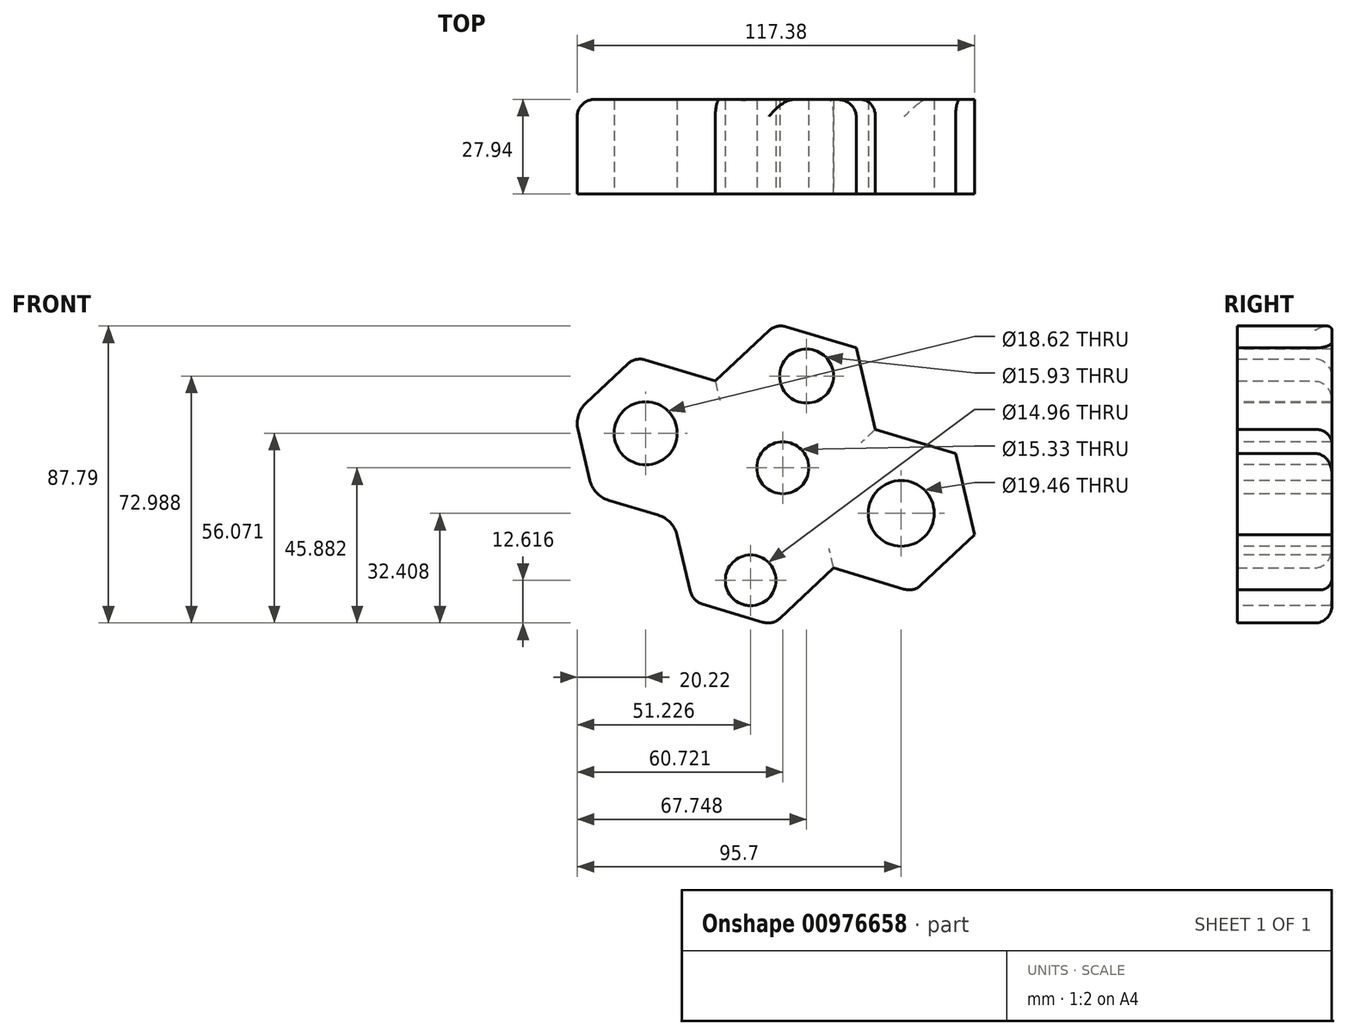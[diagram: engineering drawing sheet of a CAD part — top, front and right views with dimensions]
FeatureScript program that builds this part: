
annotation { "Feature Type Name" : "Feature", "Feature Type Description" : "" }
export const myFeature = defineFeature(function(context is Context, id is Id, definition is map)
    precondition{}
    {
        {
            var Q0;
            Q0=qCreatedBy(makeId("Front.planeOp"),FACE);
            var sketch = newSketch(context, id + "F0", { "sketchPlane" : qUnion([Q0])});
            skCircle(sketch, "E0.cCircle", {"center": v(-72.92, 28.26) * mm, "radius": 21.4 * mm, "construction": true});
            skLineSegment(sketch, "E0.0", {"start": v(-49.27, 21.14) * mm, "end": v(-67.26, 4.22) * mm});
            skLineSegment(sketch, "E0.1", {"start": v(-67.26, 4.22) * mm, "end": v(-90.91, 11.34) * mm});
            skLineSegment(sketch, "E0.2", {"start": v(-90.91, 11.34) * mm, "end": v(-96.57, 35.38) * mm});
            skLineSegment(sketch, "E0.3", {"start": v(-96.57, 35.38) * mm, "end": v(-78.57, 52.3) * mm});
            skLineSegment(sketch, "E0.4", {"start": v(-78.57, 52.3) * mm, "end": v(-54.92, 45.18) * mm});
            skLineSegment(sketch, "E0.5", {"start": v(-54.92, 45.18) * mm, "end": v(-49.27, 21.14) * mm});
            skPoint(sketch, "E0.0.midPoint", {"position": v(-58.26, 12.68) * mm});
            skLineSegment(sketch, "E1.MirrorCS", {"start": v(-36.93, 62.1) * mm, "end": v(-54.92, 45.18) * mm});
            skCircle(sketch, "E2.MirrorC", {"center": v(-31.27, 38.06) * mm, "radius": 21.4 * mm, "construction": true});
            skLineSegment(sketch, "E3.MirrorCS", {"start": v(-13.28, 54.98) * mm, "end": v(-36.93, 62.1) * mm});
            skLineSegment(sketch, "E4.MirrorCS", {"start": v(-7.62, 30.93) * mm, "end": v(-13.28, 54.98) * mm});
            skLineSegment(sketch, "E5.MirrorCS", {"start": v(-25.62, 14.01) * mm, "end": v(-7.62, 30.93) * mm});
            skLineSegment(sketch, "E6.MirrorCS", {"start": v(-49.27, 21.14) * mm, "end": v(-25.62, 14.01) * mm});
            skLineSegment(sketch, "E7.MirrorCS", {"start": v(-49.27, 21.14) * mm, "end": v(-54.92, 45.18) * mm});
            skLineSegment(sketch, "E8.MirrorCS", {"start": v(-25.62, 14.01) * mm, "end": v(-19.96, -10.03) * mm});
            skCircle(sketch, "E9.MirrorC", {"center": v(-43.61, -2.9) * mm, "radius": 21.4 * mm, "construction": true});
            skLineSegment(sketch, "E10.MirrorCS", {"start": v(-19.96, -10.03) * mm, "end": v(-37.95, -26.95) * mm});
            skLineSegment(sketch, "E11.MirrorCS", {"start": v(-37.95, -26.95) * mm, "end": v(-61.6, -19.83) * mm});
            skLineSegment(sketch, "E12.MirrorCS", {"start": v(-61.6, -19.83) * mm, "end": v(-67.26, 4.22) * mm});
            skCircle(sketch, "E13.MirrorC", {"center": v(-1.97, 6.89) * mm, "radius": 21.4 * mm, "construction": true});
            skLineSegment(sketch, "E14.MirrorCS", {"start": v(3.69, -17.15) * mm, "end": v(21.68, -0.23) * mm});
            skLineSegment(sketch, "E15.MirrorCS", {"start": v(21.68, -0.23) * mm, "end": v(16.03, 23.8) * mm});
            skLineSegment(sketch, "E16.MirrorCS", {"start": v(-7.62, 30.93) * mm, "end": v(16.03, 23.8) * mm});
            skLineSegment(sketch, "E17.MirrorCS", {"start": v(-7.62, 30.93) * mm, "end": v(-25.62, 14.01) * mm});
            skLineSegment(sketch, "E18.MirrorCS", {"start": v(-19.96, -10.03) * mm, "end": v(3.69, -17.15) * mm});
            skSolve(sketch);
        }
        {
            var Q0;
            Q0 = qSketchRegion(id + "F0", true);
            extrude(context, id + "F1", {"entities" : qUnion([Q0]), "depth" : 27.94 * mm, "offsetDistance" : 25.4 * mm});
        }
        {
            var Q0;
            Q0=makeQuery(id+"F1.opExtrude","CAP_FACE",FACE,{"disambiguationData":[OSD([sQuery(id+"F0.wireOp",EDGE,"E0.1"),sQuery(id+"F0.wireOp",EDGE,"E0.2"),sQuery(id+"F0.wireOp",EDGE,"E0.3"),sQuery(id+"F0.wireOp",EDGE,"E0.4"),sQuery(id+"F0.wireOp",EDGE,"E1.MirrorCS"),sQuery(id+"F0.wireOp",EDGE,"E3.MirrorCS"),sQuery(id+"F0.wireOp",EDGE,"E4.MirrorCS"),sQuery(id+"F0.wireOp",EDGE,"E10.MirrorCS"),sQuery(id+"F0.wireOp",EDGE,"E11.MirrorCS"),sQuery(id+"F0.wireOp",EDGE,"E12.MirrorCS"),sQuery(id+"F0.wireOp",EDGE,"E14.MirrorCS"),sQuery(id+"F0.wireOp",EDGE,"E15.MirrorCS"),sQuery(id+"F0.wireOp",EDGE,"E16.MirrorCS"),sQuery(id+"F0.wireOp",EDGE,"E18.MirrorCS")])],"isStart":false});
            var sketch = newSketch(context, id + "F2", { "sketchPlane" : qUnion([Q0])});
            skCircle(sketch, "E19", {"center": v(0, 6.09) * mm, "radius": 9.73 * mm});
            skCircle(sketch, "E20", {"center": v(-75.48, 29.75) * mm, "radius": 9.31 * mm});
            skCircle(sketch, "E21", {"center": v(-27.95, 46.67) * mm, "radius": 7.97 * mm});
            skCircle(sketch, "E22", {"center": v(-44.47, -13.7) * mm, "radius": 7.48 * mm});
            skCircle(sketch, "E23", {"center": v(-34.98, 19.56) * mm, "radius": 7.67 * mm});
            skSolve(sketch);
        }
        {
            var Q0;
            Q0 = qSketchRegion(id + "F2", true);
            extrude(context, id + "F3", {"entities" : qUnion([Q0]), "operationType" : NewBodyOperationType.REMOVE, "oppositeDirection" : true, "depth" : 54.86 * mm, "offsetDistance" : 25.4 * mm});
        }
        {
            var Q0;
            Q0=makeQuery(id+"F1.opExtrude","SWEPT_EDGE",EDGE,{"disambiguationData":[OSD([sQuery(id+"F0.wireOp",EDGE,"E0.1"),sQuery(id+"F0.wireOp",EDGE,"E12.MirrorCS"),sQuery(id+"F0.wireOp",EDGE,"E0.0")])]});
            var Q1;
            Q1=makeQuery(id+"F1.opExtrude","SWEPT_EDGE",EDGE,{"disambiguationData":[OSD([sQuery(id+"F0.wireOp",EDGE,"E0.1"),sQuery(id+"F0.wireOp",EDGE,"E0.2")])]});
            var Q2;
            Q2=makeQuery(id+"F1.opExtrude","SWEPT_EDGE",EDGE,{"disambiguationData":[OSD([sQuery(id+"F0.wireOp",EDGE,"E0.2"),sQuery(id+"F0.wireOp",EDGE,"E0.3")])]});
            fillet(context, id + "F4", {"entities" : qUnion([Q0, Q1, Q2]), "radius" : 8.2 * mm, "tangentPropagation" : true, "allowEdgeOverflow" : false});
        }
        {
            var Q0;
            Q0=makeQuery(id+"F1.opExtrude","SWEPT_EDGE",EDGE,{"disambiguationData":[OSD([sQuery(id+"F0.wireOp",EDGE,"E11.MirrorCS"),sQuery(id+"F0.wireOp",EDGE,"E12.MirrorCS")])]});
            var Q1;
            Q1=makeQuery(id+"F1.opExtrude","SWEPT_EDGE",EDGE,{"disambiguationData":[OSD([sQuery(id+"F0.wireOp",EDGE,"E0.3"),sQuery(id+"F0.wireOp",EDGE,"E0.4")])]});
            var Q2;
            Q2=makeQuery(id+"F1.opExtrude","SWEPT_EDGE",EDGE,{"disambiguationData":[OSD([sQuery(id+"F0.wireOp",EDGE,"E1.MirrorCS"),sQuery(id+"F0.wireOp",EDGE,"E3.MirrorCS")])]});
            var Q3;
            Q3=makeQuery(id+"F1.opExtrude","SWEPT_EDGE",EDGE,{"disambiguationData":[OSD([sQuery(id+"F0.wireOp",EDGE,"E10.MirrorCS"),sQuery(id+"F0.wireOp",EDGE,"E11.MirrorCS")])]});
            var Q4;
            Q4=makeQuery(id+"F1.opExtrude","SWEPT_EDGE",EDGE,{"disambiguationData":[OSD([sQuery(id+"F0.wireOp",EDGE,"E14.MirrorCS"),sQuery(id+"F0.wireOp",EDGE,"E18.MirrorCS")])]});
            var Q5;
            Q5=makeQuery(id+"F1.opExtrude","CAP_EDGE",EDGE,{"disambiguationData":[OSD([sQuery(id+"F0.wireOp",EDGE,"E10.MirrorCS")])],"isStart":true});
            var Q6;
            Q6=makeQuery(id+"F1.opExtrude","CAP_EDGE",EDGE,{"disambiguationData":[OSD([sQuery(id+"F0.wireOp",EDGE,"E4.MirrorCS")])],"isStart":true});
            var Q7;
            Q7=makeQuery(id+"F1.opExtrude","CAP_EDGE",EDGE,{"disambiguationData":[OSD([sQuery(id+"F0.wireOp",EDGE,"E16.MirrorCS")])],"isStart":true});
            var Q8;
            Q8=makeQuery(id+"F1.opExtrude","CAP_EDGE",EDGE,{"disambiguationData":[OSD([sQuery(id+"F0.wireOp",EDGE,"E1.MirrorCS")])],"isStart":true});
            var Q9;
            Q9=makeQuery(id+"F1.opExtrude","CAP_EDGE",EDGE,{"disambiguationData":[OSD([sQuery(id+"F0.wireOp",EDGE,"E0.1")])],"isStart":true});
            var Q10;
            Q10=makeQuery(id+"F1.opExtrude","CAP_EDGE",EDGE,{"disambiguationData":[OSD([sQuery(id+"F0.wireOp",EDGE,"E11.MirrorCS")])],"isStart":true});
            var Q11;
            Q11=makeQuery(id+"F1.opExtrude","CAP_EDGE",EDGE,{"disambiguationData":[OSD([sQuery(id+"F0.wireOp",EDGE,"E0.4")])],"isStart":true});
            var Q12;
            Q12=makeQuery(id+"F1.opExtrude","CAP_EDGE",EDGE,{"disambiguationData":[OSD([sQuery(id+"F0.wireOp",EDGE,"E18.MirrorCS")])],"isStart":true});
            fillet(context, id + "F5", {"entities" : qUnion([Q0, Q1, Q2, Q3, Q4, Q5, Q6, Q7, Q8, Q9, Q10, Q11, Q12]), "radius" : 5.08 * mm, "tangentPropagation" : true, "allowEdgeOverflow" : false});
        }
    });
